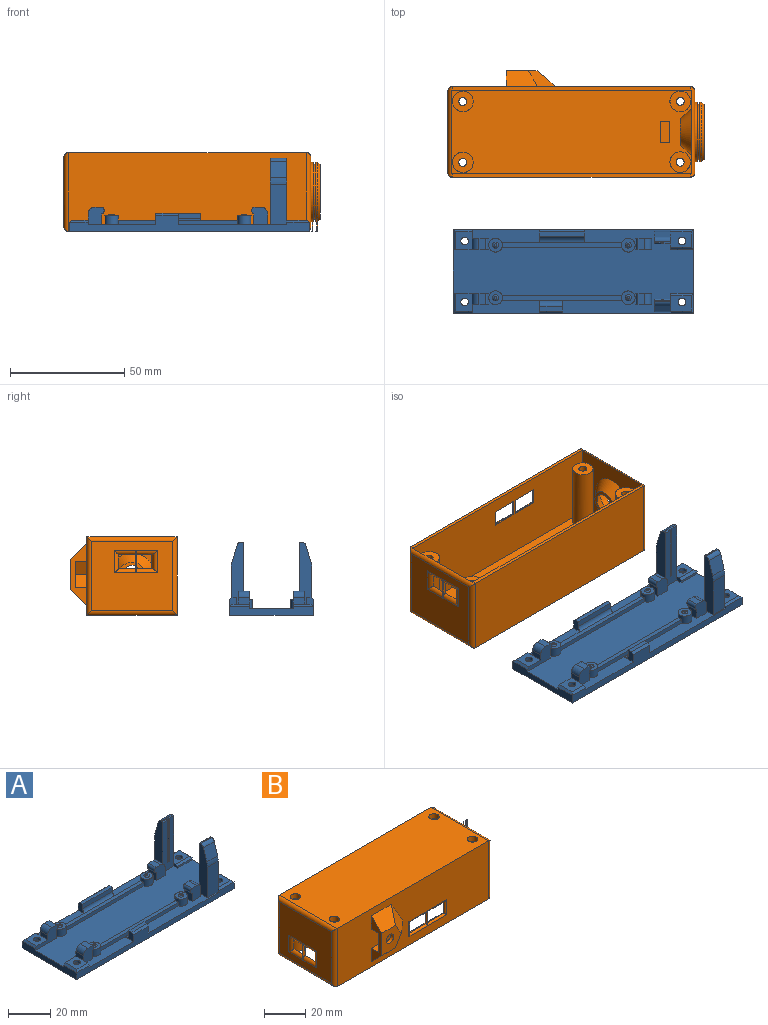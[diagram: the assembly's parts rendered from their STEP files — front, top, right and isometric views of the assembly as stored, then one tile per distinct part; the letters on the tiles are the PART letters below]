
ASSEMBLY  parts=2 mates=1
PART A: 175 faces, bbox 105x36.6x32.1 mm
  f0: cylinder r=1.68mm len=3.35mm, axis (0,0,-1), area 15.8mm2, adj f98,f115
  f1: cylinder r=1.68mm len=3.35mm, axis (0,0,-1), area 15.8mm2, adj f100,f136
  f2: cylinder r=1.68mm len=3.35mm, axis (0,0,-1), area 15.8mm2, adj f108,f129
  f3: cylinder r=1.68mm len=3.35mm, axis (0,0,-1), area 15.8mm2, adj f104,f122
  f4: plane 105x36.6mm, normal (0,0,-1), area 3729.8mm2, adj f38,f39,f40,f41,f109,f110,f111,f112
  f5: plane 27.4x5.5mm, normal (1,0,0), area 133.6mm2, adj f10,f15,f16,f74,f75,f77,f108,f148
  f6: plane 105x36.6mm, normal (0,0,1), area 2837.8mm2, adj f8,f9,f10,f11,f15,f20,f21,f23
  f7: plane 5x2.65mm, normal (-1,0,0), area 13.3mm2, adj f29,f30,f80,f100
  f8: cylinder r=3mm len=6mm, axis (0,0,-1), area 71.3mm2, adj f6,f47,f94,f95,f96
  f9: cylinder r=3mm len=6mm, axis (0,0,-1), area 71.3mm2, adj f6,f42,f91,f92,f93
  f10: plane 17.63x7.2mm, normal (0,1,0), area 127mm2, adj f5,f6,f11,f77,f107
  f11: plane 29.1x5.5mm, normal (-1,0,0), area 144.5mm2, adj f6,f10,f15,f16,f72,f74,f75,f77
  f12: plane 25.1x0.5mm, normal (1,0,0), area 12.5mm2, adj f13,f15,f69,f72
  f13: plane 25.1x1.2mm, normal (0,-1,0), area 30.1mm2, adj f12,f14,f16,f69
  f14: plane 25.1x0.5mm, normal (-1,0,0), area 12.6mm2, adj f13,f15,f16,f69
  f15: plane 29.1x7.2mm, normal (0,-1,0), area 177.9mm2, adj f5,f6,f11,f12,f14,f16,f69,f72
  f16: plane 7.2x1.01mm, normal (0,0,1), area 5.2mm2, adj f5,f11,f13,f14,f15,f72,f75
  f17: plane 1x0.5mm, normal (-1,0,0), area 0.4mm2, adj f18,f23,f66,f71
  f18: plane 1.21x1.01mm, normal (0,1,0), area 1.2mm2, adj f17,f19,f67,f71
  f19: plane 1x0.5mm, normal (1,0,0), area 0.4mm2, adj f18,f23,f68,f71
  f20: plane 29.1x5.5mm, normal (-1,0,0), area 144.5mm2, adj f6,f21,f23,f24,f71,f73,f76,f78
  f21: plane 17.63x7.2mm, normal (0,-1,0), area 127mm2, adj f6,f20,f22,f78,f103
  f22: plane 27.4x5.5mm, normal (1,0,0), area 133.5mm2, adj f21,f23,f24,f71,f73,f76,f78,f104
  f23: plane 28.6x7.2mm, normal (0,1,0), area 176.4mm2, adj f6,f17,f19,f20,f22,f66,f68,f70
  f24: plane 7.2x0.51mm, normal (0,0,1), area 3.7mm2, adj f20,f22,f71,f76
  f25: plane 7.65x7mm, normal (0,1,0), area 46.1mm2, adj f6,f33,f37,f56,f65,f82,f97
  f26: plane 15.25x7.65mm, normal (0,-1,0), area 62.1mm2, adj f6,f33,f37,f39,f56,f65,f82,f98
  f27: plane 7.65x7mm, normal (0,1,0), area 46.1mm2, adj f6,f36,f57,f58,f64,f81
  f28: plane 7.65x7mm, normal (0,-1,0), area 46.1mm2, adj f6,f36,f57,f58,f64,f81
  f29: plane 15.25x7.65mm, normal (0,1,0), area 62.1mm2, adj f6,f7,f34,f39,f59,f63,f80,f100
  f30: plane 7.65x7mm, normal (0,-1,0), area 46.1mm2, adj f6,f7,f34,f59,f63,f80,f99
  f31: plane 7.65x7mm, normal (0,1,0), area 46.1mm2, adj f6,f35,f60,f61,f62,f79
  f32: plane 7.65x7mm, normal (0,-1,0), area 46.1mm2, adj f6,f35,f60,f61,f62,f79
  f33: plane 5x3mm, normal (0,0,1), area 15mm2, adj f25,f26,f65,f82
  f34: plane 5x3mm, normal (0,0,1), area 15mm2, adj f29,f30,f63,f80
  f35: plane 5x4.65mm, normal (-1,0,0), area 23.3mm2, adj f6,f31,f32,f62
  f36: plane 5x4.65mm, normal (-1,0,0), area 23.3mm2, adj f6,f27,f28,f64
  f37: plane 5x4.65mm, normal (1,0,0), area 23.3mm2, adj f6,f25,f26,f65
  f38: plane 105x7mm, normal (0,1,0), area 413.1mm2, adj f4,f6,f39,f41,f83,f85,f97,f107
  f39: plane 36.6x4mm, normal (-1,0,0), area 127.4mm2, adj f4,f6,f26,f29,f38,f40,f141,f144
  f40: plane 105x7mm, normal (0,-1,0), area 373.1mm2, adj f4,f6,f39,f41,f88,f89,f99,f103
  f41: plane 36.6x4mm, normal (1,0,0), area 127.4mm2, adj f4,f6,f38,f40,f102,f106,f139,f147
  f42: plane 6x6mm, normal (0,0,1), area 23mm2, adj f9,f55
  f43: cylinder r=3mm len=6mm, axis (0,0,-1), area 71.3mm2, adj f6,f44,f91,f92,f93
  f44: plane 6x6mm, normal (0,0,1), area 23mm2, adj f43,f54
  f45: cylinder r=3mm len=6mm, axis (0,0,-1), area 71.3mm2, adj f6,f46,f94,f95,f96
  f46: plane 6x6mm, normal (0,0,1), area 23mm2, adj f45,f53
  f47: plane 6x6mm, normal (0,0,1), area 23mm2, adj f8,f52
  f48: plane 1.19x1.19mm, normal (0,0,1), area 1.1mm2, adj f55
  f49: plane 1.19x1.19mm, normal (0,0,1), area 1.1mm2, adj f54
  f50: plane 1.19x1.19mm, normal (0,0,1), area 1.1mm2, adj f52
  f51: plane 1.19x1.19mm, normal (0,0,1), area 1.1mm2, adj f53
  f52: torus R=0.59mm, axis (0,0,-1), area 5.8mm2, adj f47,f50
  f53: torus R=0.59mm, axis (0,0,-1), area 5.8mm2, adj f46,f51
  f54: torus R=0.59mm, axis (0,0,-1), area 5.8mm2, adj f44,f49
  f55: torus R=0.59mm, axis (0,0,-1), area 5.8mm2, adj f42,f48
  f56: plane 5x2.65mm, normal (-1,0,0), area 13.3mm2, adj f25,f26,f82,f98
  f57: plane 5x4.65mm, normal (1,0,0), area 23.3mm2, adj f6,f27,f28,f81
  f58: plane 5x3mm, normal (0,0,1), area 15mm2, adj f27,f28,f64,f81
  f59: plane 5x4.65mm, normal (1,0,0), area 23.3mm2, adj f6,f29,f30,f63
  f60: plane 5x4.65mm, normal (1,0,0), area 23.3mm2, adj f6,f31,f32,f79
  f61: plane 5x3mm, normal (0,0,1), area 15mm2, adj f31,f32,f62,f79
  f62: cylinder r=1.62mm len=5mm, axis (0,1,0), area 19.1mm2, adj f31,f32,f35,f61
  f63: cylinder r=1.62mm len=5mm, axis (0,1,0), area 19.1mm2, adj f29,f30,f34,f59
  f64: cylinder r=1.62mm len=5mm, axis (0,1,0), area 19.1mm2, adj f27,f28,f36,f58
  f65: cylinder r=1.62mm len=5mm, axis (0,1,0), area 19.1mm2, adj f25,f26,f33,f37
  f66: plane 24.11x0.5mm, normal (-1,0,0), area 12mm2, adj f17,f23,f67,f70
  f67: plane 24.11x1.21mm, normal (0,1,0), area 28.9mm2, adj f18,f66,f68,f70
  f68: plane 24.1x0.5mm, normal (1,0,0), area 12.1mm2, adj f19,f23,f67,f70
  f69: plane 1.2x0.5mm, normal (0,0,1), area 0.6mm2, adj f12,f13,f14,f15
  f70: plane 1.2x0.5mm, normal (0,0,1), area 0.6mm2, adj f23,f66,f67,f68
  f71: cylinder r=0.5mm len=7.2mm, axis (1,0,0), area 4.7mm2, adj f17,f18,f19,f20,f22,f23,f24
  f72: cylinder r=0.5mm len=3mm, axis (-1,0,0), area 2.4mm2, adj f11,f12,f15,f16
  f73: plane 7.2x7.17mm, normal (0,-0.96,0.29), area 53.9mm2, adj f20,f22,f76,f78
  f74: plane 7.2x7.17mm, normal (0,0.96,0.29), area 53.9mm2, adj f5,f11,f75,f77
  f75: cylinder r=2mm len=7.2mm, axis (-1,0,0), area 18.4mm2, adj f5,f11,f16,f74
  f76: cylinder r=2mm len=7.2mm, axis (-1,0,0), area 18.4mm2, adj f20,f22,f24,f73
  f77: cylinder r=10mm len=7.2mm, axis (-1,0,0), area 21mm2, adj f5,f10,f11,f74
  f78: cylinder r=10mm len=7.2mm, axis (1,0,0), area 21mm2, adj f20,f21,f22,f73
  f79: cylinder r=3mm len=5mm, axis (0,-1,0), area 23.6mm2, adj f31,f32,f60,f61
  f80: cylinder r=3mm len=5mm, axis (0,1,0), area 23.6mm2, adj f7,f29,f30,f34
  f81: cylinder r=3mm len=5mm, axis (0,-1,0), area 23.6mm2, adj f27,f28,f57,f58
  f82: cylinder r=3mm len=5mm, axis (0,1,0), area 23.6mm2, adj f25,f26,f33,f56
  f83: plane 5.5x5mm, normal (-1,0,0), area 15.8mm2, adj f6,f38,f84,f86,f145,f150
  f84: plane 20x2.5mm, normal (0,-1,0), area 50mm2, adj f83,f85,f86,f150
  f85: plane 5.5x5mm, normal (1,0,0), area 15.8mm2, adj f6,f38,f84,f86,f145,f150
  f86: plane 20x2mm, normal (0,0,1), area 40mm2, adj f83,f84,f85,f145
  f87: plane 10x2.5mm, normal (0,1,0), area 25mm2, adj f88,f89,f90,f149
  f88: plane 5.5x5mm, normal (-1,0,0), area 15.8mm2, adj f6,f40,f87,f90,f140,f149
  f89: plane 5.5x5mm, normal (1,0,0), area 15.8mm2, adj f6,f40,f87,f90,f140,f149
  f90: plane 10x2mm, normal (0,0,1), area 20mm2, adj f87,f88,f89,f140
  f91: plane 52.34x2mm, normal (0,1,0), area 104.7mm2, adj f6,f9,f43,f93
  f92: plane 52.34x2mm, normal (0,-1,0), area 104.7mm2, adj f6,f9,f43,f93
  f93: plane 52.34x2mm, normal (0,0,1), area 104.2mm2, adj f9,f43,f91,f92
  f94: plane 52.34x2mm, normal (0,1,0), area 104.7mm2, adj f6,f8,f45,f96
  f95: plane 52.34x2mm, normal (0,-1,0), area 104.7mm2, adj f6,f8,f45,f96
  f96: plane 52.34x2mm, normal (0,0,1), area 104.2mm2, adj f8,f45,f94,f95
  f97: plane 3.8x2mm, normal (1,0,0), area 7.1mm2, adj f6,f25,f38,f98,f143
  f98: plane 7.8x7.25mm, normal (0,0,1), area 47.7mm2, adj f0,f26,f56,f97,f143,f144
  f99: plane 3.8x2mm, normal (1,0,0), area 7.1mm2, adj f6,f30,f40,f100,f142
  f100: plane 7.8x7.25mm, normal (0,0,1), area 47.7mm2, adj f1,f7,f29,f99,f141,f142
  f101: plane 2.6x2mm, normal (-1,0,0), area 4.7mm2, adj f6,f23,f102,f104,f137
  f102: plane 9.9x1mm, normal (0,1,0), area 9.9mm2, adj f6,f41,f101,f137
  f103: plane 1.7x0.7mm, normal (-1,0,0), area 0.9mm2, adj f6,f21,f40,f138
  f104: plane 8.9x6.8mm, normal (0,0,1), area 51.7mm2, adj f3,f22,f101,f137,f138,f139
  f105: plane 2.6x2mm, normal (-1,0,0), area 4.7mm2, adj f6,f15,f106,f108,f146
  f106: plane 9.9x1mm, normal (0,-1,0), area 9.9mm2, adj f6,f41,f105,f146
  f107: plane 1.7x0.7mm, normal (-1,0,0), area 0.9mm2, adj f6,f10,f38,f148
  f108: plane 8.9x6.8mm, normal (0,0,1), area 51.7mm2, adj f2,f5,f105,f146,f147,f148
  f109: plane 2.86x2.5mm, normal (-0.5,-0.87,0), area 8.3mm2, adj f4,f110,f114,f172
  f110: plane 3.3x2.5mm, normal (-1,0,0), area 8.2mm2, adj f4,f109,f111,f170
  f111: plane 2.86x2.5mm, normal (-0.5,0.87,0), area 8.3mm2, adj f4,f110,f112,f169
  f112: plane 2.86x2.5mm, normal (0.5,0.87,0), area 8.3mm2, adj f4,f111,f113,f171
  f113: plane 3.3x2.5mm, normal (1,0,0), area 8.2mm2, adj f4,f112,f114,f173
  f114: plane 2.86x2.5mm, normal (0.5,-0.87,0), area 8.3mm2, adj f4,f109,f113,f174
  f115: plane 4.29x3.72mm, normal (0,0,-1), area 3.1mm2, adj f0,f169,f170,f171,f172,f173,f174
  f116: plane 2.86x2.5mm, normal (0.5,-0.87,0), area 8.3mm2, adj f4,f117,f121,f161
  f117: plane 2.86x2.5mm, normal (-0.5,-0.87,0), area 8.3mm2, adj f4,f116,f118,f162
  f118: plane 3.3x2.5mm, normal (-1,0,0), area 8.2mm2, adj f4,f117,f119,f160
  f119: plane 2.86x2.5mm, normal (-0.5,0.87,0), area 8.3mm2, adj f4,f118,f120,f158
  f120: plane 2.86x2.5mm, normal (0.5,0.87,0), area 8.3mm2, adj f4,f119,f121,f157
  f121: plane 3.3x2.5mm, normal (1,0,0), area 8.2mm2, adj f4,f116,f120,f159
  f122: plane 4.29x3.72mm, normal (0,0,-1), area 3.1mm2, adj f3,f157,f158,f159,f160,f161,f162
  f123: plane 3.3x2.5mm, normal (1,0,0), area 8.2mm2, adj f4,f124,f128,f152
  f124: plane 2.86x2.5mm, normal (0.5,-0.87,0), area 8.3mm2, adj f4,f123,f125,f154
  f125: plane 2.86x2.5mm, normal (-0.5,-0.87,0), area 8.3mm2, adj f4,f124,f126,f156
  f126: plane 3.3x2.5mm, normal (-1,0,0), area 8.2mm2, adj f4,f125,f127,f155
  f127: plane 2.86x2.5mm, normal (-0.5,0.87,0), area 8.3mm2, adj f4,f126,f128,f153
  f128: plane 2.86x2.5mm, normal (0.5,0.87,0), area 8.3mm2, adj f4,f123,f127,f151
  f129: plane 4.29x3.72mm, normal (0,0,-1), area 3.1mm2, adj f2,f151,f152,f153,f154,f155,f156
  f130: plane 2.86x2.5mm, normal (-0.5,0.87,0), area 8.3mm2, adj f4,f131,f135,f163
  f131: plane 2.86x2.5mm, normal (0.5,0.87,0), area 8.3mm2, adj f4,f130,f132,f164
  f132: plane 3.3x2.5mm, normal (1,0,0), area 8.2mm2, adj f4,f131,f133,f166
  f133: plane 2.86x2.5mm, normal (0.5,-0.87,0), area 8.3mm2, adj f4,f132,f134,f168
  f134: plane 2.86x2.5mm, normal (-0.5,-0.87,0), area 8.3mm2, adj f4,f133,f135,f167
  f135: plane 3.3x2.5mm, normal (-1,0,0), area 8.2mm2, adj f4,f130,f134,f165
  f136: plane 4.29x3.72mm, normal (0,0,-1), area 3.1mm2, adj f1,f163,f164,f165,f166,f167,f168
  f137: plane 9.9x1mm, normal (0,0.71,0.71), area 13.3mm2, adj f101,f102,f104,f139
  f138: plane 9.9x1mm, normal (0,-0.71,0.71), area 13.3mm2, adj f22,f40,f103,f104,f139
  f139: plane 8.8x1mm, normal (0.71,0,0.71), area 11mm2, adj f41,f104,f137,f138
  f140: plane 10x1mm, normal (0,-0.71,0.71), area 14.1mm2, adj f40,f88,f89,f90
  f141: plane 8.8x1mm, normal (-0.71,0,0.71), area 11.7mm2, adj f29,f39,f100,f142
  f142: plane 8.25x1mm, normal (0,-0.71,0.71), area 11mm2, adj f40,f99,f100,f141
  f143: plane 8.25x1mm, normal (0,0.71,0.71), area 11mm2, adj f38,f97,f98,f144
  f144: plane 8.8x1mm, normal (-0.71,0,0.71), area 11.7mm2, adj f26,f39,f98,f143
  f145: plane 20x1mm, normal (0,0.71,0.71), area 28.3mm2, adj f38,f83,f85,f86
  f146: plane 9.9x1mm, normal (0,-0.71,0.71), area 13.3mm2, adj f105,f106,f108,f147
  f147: plane 8.8x1mm, normal (0.71,0,0.71), area 11mm2, adj f41,f108,f146,f148
  f148: plane 9.9x1mm, normal (0,0.71,0.71), area 13.3mm2, adj f5,f38,f107,f108,f147
  f149: cylinder r=2.5mm len=10mm, axis (-1,0,0), area 39.3mm2, adj f6,f87,f88,f89
  f150: cylinder r=2.5mm len=20mm, axis (1,0,0), area 78.5mm2, adj f6,f83,f84,f85
  f151: plane 2.86x2.23mm, normal (0.35,0.61,-0.71), area 3.9mm2, adj f128,f129,f152,f153
  f152: plane 3.3x1mm, normal (0.71,0,-0.71), area 3.9mm2, adj f123,f129,f151,f154
  f153: plane 2.86x2.23mm, normal (-0.35,0.61,-0.71), area 3.9mm2, adj f127,f129,f151,f155
  f154: plane 2.86x2.23mm, normal (0.35,-0.61,-0.71), area 3.9mm2, adj f124,f129,f152,f156
  f155: plane 3.3x1mm, normal (-0.71,0,-0.71), area 3.9mm2, adj f126,f129,f153,f156
  f156: plane 2.86x2.23mm, normal (-0.35,-0.61,-0.71), area 3.9mm2, adj f125,f129,f154,f155
  f157: plane 2.86x2.23mm, normal (0.35,0.61,-0.71), area 3.9mm2, adj f120,f122,f158,f159
  f158: plane 2.86x2.23mm, normal (-0.35,0.61,-0.71), area 3.9mm2, adj f119,f122,f157,f160
  f159: plane 3.3x1mm, normal (0.71,0,-0.71), area 3.9mm2, adj f121,f122,f157,f161
  f160: plane 3.3x1mm, normal (-0.71,0,-0.71), area 3.9mm2, adj f118,f122,f158,f162
  f161: plane 2.86x2.23mm, normal (0.35,-0.61,-0.71), area 3.9mm2, adj f116,f122,f159,f162
  f162: plane 2.86x2.23mm, normal (-0.35,-0.61,-0.71), area 3.9mm2, adj f117,f122,f160,f161
  f163: plane 2.86x2.23mm, normal (-0.35,0.61,-0.71), area 3.9mm2, adj f130,f136,f164,f165
  f164: plane 2.86x2.23mm, normal (0.35,0.61,-0.71), area 3.9mm2, adj f131,f136,f163,f166
  f165: plane 3.3x1mm, normal (-0.71,0,-0.71), area 3.9mm2, adj f135,f136,f163,f167
  f166: plane 3.3x1mm, normal (0.71,0,-0.71), area 3.9mm2, adj f132,f136,f164,f168
  f167: plane 2.86x2.23mm, normal (-0.35,-0.61,-0.71), area 3.9mm2, adj f134,f136,f165,f168
  f168: plane 2.86x2.23mm, normal (0.35,-0.61,-0.71), area 3.9mm2, adj f133,f136,f166,f167
  f169: plane 2.86x2.23mm, normal (-0.35,0.61,-0.71), area 3.9mm2, adj f111,f115,f170,f171
  f170: plane 3.3x1mm, normal (-0.71,0,-0.71), area 3.9mm2, adj f110,f115,f169,f172
  f171: plane 2.86x2.23mm, normal (0.35,0.61,-0.71), area 3.9mm2, adj f112,f115,f169,f173
  f172: plane 2.86x2.23mm, normal (-0.35,-0.61,-0.71), area 3.9mm2, adj f109,f115,f170,f174
  f173: plane 3.3x1mm, normal (0.71,0,-0.71), area 3.9mm2, adj f113,f115,f171,f174
  f174: plane 2.86x2.23mm, normal (0.35,-0.61,-0.71), area 3.9mm2, adj f114,f115,f172,f173
PART B: 100 faces, bbox 114x48.6x36.5 mm
  f0: extruded ~25.99x25.99mm, area 81mm2, adj f3,f91,f98
  f1: plane 36.6x32.94mm, normal (1,0,0), area 1116.7mm2, adj f6,f12,f13,f46,f83,f84,f85,f86
  f2: plane 35.6x30.5mm, normal (-1,0,0), area 901.4mm2, adj f45,f46,f47,f48,f83,f84,f85,f86
  f3: plane 35.6x30.5mm, normal (1,0,0), area 554.9mm2, adj f0,f49,f50,f51,f52
  f4: plane 104x34.5mm, normal (0,-1,0), area 2995.6mm2, adj f11,f17,f48,f49,f53,f54,f57,f58
  f5: plane 104x1.5mm, normal (0,0,-1), area 156mm2, adj f13,f15,f46,f50
  f6: plane 105x33mm, normal (0,1,0), area 3304.7mm2, adj f1,f12,f14,f17,f37,f38,f39,f40
  f7: cylinder r=1.75mm len=26.5mm, axis (0,0,1), area 291.4mm2, adj f24,f34,f35
  f8: cylinder r=1.75mm len=26.5mm, axis (0,0,1), area 291.4mm2, adj f22,f31,f32
  f9: cylinder r=1.75mm len=26.5mm, axis (0,0,1), area 291.4mm2, adj f20,f29
  f10: cylinder r=1.75mm len=26.5mm, axis (0,0,1), area 291.4mm2, adj f18,f26,f27
  f11: plane 104x39.6mm, normal (0,0,1), area 4039.9mm2, adj f4,f15,f28,f30,f33,f36,f47,f51
  f12: plane 105x36.6mm, normal (0,0,-1), area 3548.1mm2, adj f1,f6,f13,f14,f19,f21,f23,f25
  f13: plane 105x33mm, normal (0,-1,0), area 3465mm2, adj f1,f5,f12,f14,f46,f50
  f14: plane 36.6x32.94mm, normal (-1,0,0), area 888.8mm2, adj f6,f12,f13,f50,f72
  f15: plane 104x34.5mm, normal (0,1,0), area 3588mm2, adj f5,f11,f45,f52
  f16: plane 22.02x22.02mm, normal (1,0,0), area 65.9mm2, adj f73,f75
  f17: plane 104x1.5mm, normal (0,0,-1), area 156mm2, adj f4,f6,f46,f50
  f18: plane 9x9mm, normal (0,0,-1), area 54mm2, adj f10,f19
  f19: cylinder r=4.5mm len=28mm, axis (0,0,1), area 791.7mm2, adj f12,f18
  f20: plane 9x9mm, normal (0,0,-1), area 54mm2, adj f9,f21
  f21: cylinder r=4.5mm len=28mm, axis (0,0,1), area 791.7mm2, adj f12,f20
  f22: plane 9x9mm, normal (0,0,-1), area 54mm2, adj f8,f23
  f23: cylinder r=4.5mm len=28mm, axis (0,0,1), area 791.7mm2, adj f12,f22
  f24: plane 9x9mm, normal (0,0,-1), area 54mm2, adj f7,f25
  f25: cylinder r=4.5mm len=28mm, axis (0,0,1), area 791.7mm2, adj f12,f24
  f26: cone r=0mm half-angle=59deg, axis (0,0,1), area 0mm2, adj f10,f27
  f27: plane 5x5mm, normal (0,0,1), area 9.7mm2, adj f10,f26,f28
  f28: cylinder r=2.5mm len=5mm, axis (0,0,1), area 47.1mm2, adj f11,f27
  f29: plane 5x5mm, normal (0,0,1), area 10mm2, adj f9,f30
  f30: cylinder r=2.5mm len=5mm, axis (0,0,1), area 47.1mm2, adj f11,f29
  f31: cone r=0mm half-angle=59deg, axis (0,0,1), area 0mm2, adj f8,f32
  f32: plane 5.78x5.78mm, normal (0,0,1), area 9.7mm2, adj f8,f31,f33
  f33: cylinder r=2.5mm len=5mm, axis (0,0,1), area 47.1mm2, adj f11,f32
  f34: cone r=0mm half-angle=59deg, axis (0,0,1), area 0mm2, adj f7,f35
  f35: plane 5.78x5.78mm, normal (0,0,1), area 9.7mm2, adj f7,f34,f36
  f36: cylinder r=2.5mm len=5mm, axis (0,0,1), area 47.1mm2, adj f11,f35
  f37: plane 11.5x0.5mm, normal (0,0,1), area 5.8mm2, adj f6,f38,f40,f53
  f38: plane 6.97x0.5mm, normal (-1,0,0), area 3.5mm2, adj f6,f37,f39,f56
  f39: plane 11.5x0.5mm, normal (0,0,-1), area 5.8mm2, adj f6,f38,f40,f58
  f40: plane 6.97x0.5mm, normal (1,0,0), area 3.5mm2, adj f6,f37,f39,f57
  f41: plane 11.5x0.5mm, normal (0,0,1), area 5.8mm2, adj f6,f42,f44,f53
  f42: plane 6.97x0.5mm, normal (-1,0,0), area 3.5mm2, adj f6,f41,f43,f54
  f43: plane 11.5x0.5mm, normal (0,0,-1), area 5.8mm2, adj f6,f42,f44,f58
  f44: plane 6.97x0.5mm, normal (1,0,0), area 3.5mm2, adj f6,f41,f43,f55
  f45: cylinder r=2mm len=34.5mm, axis (0,0,-1), area 102.1mm2, adj f2,f15,f46,f47
  f46: cylinder r=2mm len=39.6mm, axis (0,-1,0), area 101.3mm2, adj f1,f2,f5,f6,f13,f17,f45,f48
  f47: cylinder r=2mm len=39.6mm, axis (0,-1,0), area 118.1mm2, adj f2,f11,f45,f48
  f48: cylinder r=2mm len=34.5mm, axis (0,0,1), area 102.1mm2, adj f2,f4,f46,f47
  f49: cylinder r=2mm len=34.5mm, axis (0,0,-1), area 102.1mm2, adj f3,f4,f50,f51
  f50: cylinder r=2mm len=39.6mm, axis (0,1,0), area 101.3mm2, adj f3,f5,f6,f13,f14,f17,f49,f52
  f51: cylinder r=2mm len=39.6mm, axis (0,1,0), area 118.1mm2, adj f3,f11,f49,f52
  f52: cylinder r=2mm len=34.5mm, axis (0,0,1), area 102.1mm2, adj f3,f15,f50,f51
  f53: cylinder r=1mm len=26mm, axis (-1,0,0), area 38.7mm2, adj f4,f37,f41,f54,f55,f56,f57
  f54: cylinder r=1mm len=8.97mm, axis (0,0,-1), area 12.5mm2, adj f4,f42,f53,f58
  f55: cylinder r=1mm len=7.97mm, axis (0,0,1), area 7.8mm2, adj f44,f53,f56,f58
  f56: cylinder r=1mm len=7.97mm, axis (0,0,-1), area 7.8mm2, adj f38,f53,f55,f58
  f57: cylinder r=1mm len=8.97mm, axis (0,0,1), area 12.5mm2, adj f4,f40,f53,f58
  f58: cylinder r=1mm len=26mm, axis (1,0,0), area 38.7mm2, adj f4,f39,f43,f54,f55,f56,f57
  f59: plane 27.3x7mm, normal (-1,0,0), area 85.6mm2, adj f4,f60,f63,f64,f65,f78,f79
  f60: plane 9x5mm, normal (0,0,-1), area 45mm2, adj f4,f59,f61,f65
  f61: plane 5.65x5mm, normal (-0.87,0,-0.5), area 32.6mm2, adj f4,f60,f62,f65
  f62: plane 5.65x5mm, normal (-0.87,0,0.5), area 32.6mm2, adj f4,f61,f63,f65
  f63: plane 9x5mm, normal (0,0,1), area 45mm2, adj f4,f59,f62,f65
  f64: plane 13.42x13.3mm, normal (0,-1,0), area 132.5mm2, adj f59,f66,f78,f79,f80,f81
  f65: plane 12.26x11.3mm, normal (0,1,0), area 99.7mm2, adj f59,f60,f61,f62,f63,f66
  f66: cylinder r=2.55mm len=5.1mm, axis (0,-1,0), area 32mm2, adj f64,f65
  f67: plane 4.28x1.7mm, normal (0,1,0), area 7.3mm2, adj f12,f68,f70,f71
  f68: plane 9.44x1.7mm, normal (1,0,0), area 16mm2, adj f12,f67,f69,f71
  f69: plane 4.28x1.7mm, normal (0,-1,0), area 7.3mm2, adj f12,f68,f70,f71
  f70: plane 9.44x1.7mm, normal (-1,0,0), area 16mm2, adj f12,f67,f69,f71
  f71: plane 9.44x4.28mm, normal (0,0,-1), area 40.4mm2, adj f67,f68,f69,f70
  f72: offset ~22.06x22.06mm, area 320.4mm2, adj f14,f74
  f73: bspline ~19.99x19.98mm, area 387.9mm2, adj f16,f74
  f74: bspline ~11.81x11.81mm, area 46.3mm2, adj f72,f73
  f75: extruded ~21.99x21.99mm, area 276.4mm2, adj f16,f77
  f76: extruded ~25.99x25.99mm, area 82.1mm2, adj f82,f92,f94,f96
  f77: plane 24.14x24.14mm, normal (1,0,0), area 72.5mm2, adj f75,f82
  f78: plane 13.62x7mm, normal (0,-0.71,0.71), area 114.8mm2, adj f4,f59,f64,f81
  f79: plane 13.62x7mm, normal (0,-0.71,-0.71), area 114.8mm2, adj f4,f59,f64,f80
  f80: plane 13.65x11.92mm, normal (0.61,-0.71,-0.35), area 116mm2, adj f4,f64,f79,f81
  f81: plane 13.65x11.92mm, normal (0.61,-0.71,0.35), area 116mm2, adj f4,f64,f78,f80
  f82: bspline ~25.99x25.98mm, area 111.1mm2, adj f76,f77
  f83: plane 9.87x1.5mm, normal (0,-1,0), area 10.5mm2, adj f1,f2,f85,f87
  f84: plane 9.87x1.5mm, normal (0,1,0), area 10.5mm2, adj f1,f2,f88,f90
  f85: cylinder r=2mm len=9.34mm, axis (0,-1,0), area 22.1mm2, adj f1,f2,f83,f86
  f86: cylinder r=2mm len=9.87mm, axis (0,0,1), area 20.9mm2, adj f1,f2,f85,f87
  f87: cylinder r=2mm len=9.34mm, axis (0,-1,0), area 22.1mm2, adj f1,f2,f83,f86
  f88: cylinder r=2mm len=9.34mm, axis (0,-1,0), area 22.1mm2, adj f1,f2,f84,f89
  f89: cylinder r=2mm len=9.87mm, axis (0,0,1), area 20.9mm2, adj f1,f2,f88,f90
  f90: cylinder r=2mm len=9.34mm, axis (0,-1,0), area 22.1mm2, adj f1,f2,f84,f89
  f91: plane 26x26mm, normal (1,0,0), area 69.3mm2, adj f0,f93
  f92: plane 26x26mm, normal (-1,0,0), area 69.3mm2, adj f76,f93
  f93: cylinder r=12.12mm len=24.24mm, axis (1,0,0), area 76.2mm2, adj f91,f92
  f94: cylinder r=0.15mm len=4.25mm, axis (0,0,1), area 4mm2, adj f76,f95
  f95: plane 0.3x0.3mm, normal (0,0,1), area 0.1mm2, adj f94
  f96: cylinder r=0.15mm len=4.25mm, axis (0,0,1), area 4mm2, adj f76,f97
  f97: plane 0.3x0.3mm, normal (0,0,1), area 0.1mm2, adj f96
  f98: cylinder r=0.15mm len=4.25mm, axis (0,0,1), area 4mm2, adj f0,f99
  f99: plane 0.3x0.3mm, normal (0,0,1), area 0.1mm2, adj f98
PLACE A rot(axis=(-1,0,0),0deg) t=(-69.33,-53.12,13.22)mm
PLACE B rot(axis=(1,0,0),180deg) t=(-70.17,7.86,17.35)mm
MATE planar A.f4 <-> B.f11  axis (0,0,-1) through (-64.33,-34.82,-1.98)mm
